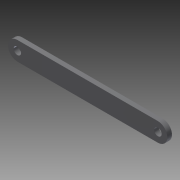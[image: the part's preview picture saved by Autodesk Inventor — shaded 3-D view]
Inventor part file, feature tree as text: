
AUTODESK INVENTOR PART (.ipt)
format: ipt  version: 2015 (Build 190159000, 159)  size: 93,184 bytes
history: native  units: mm
features: extrude x1, sketch x1
ambient origin geometry x8: Origin, YZ Plane, XZ Plane, XY Plane, X Axis, Y Axis, Z Axis, Center Point
bodies: Solid1 (feature_tree)
feature tree (2):
  extrude  "Extrusion1"  Depth=20.0mm
  sketch  "Sketch1"  dims[d0=150.0mm d1=20.0mm d2=8.0mm d3=8.0mm d4=5.0mm d5=0.0mm]
